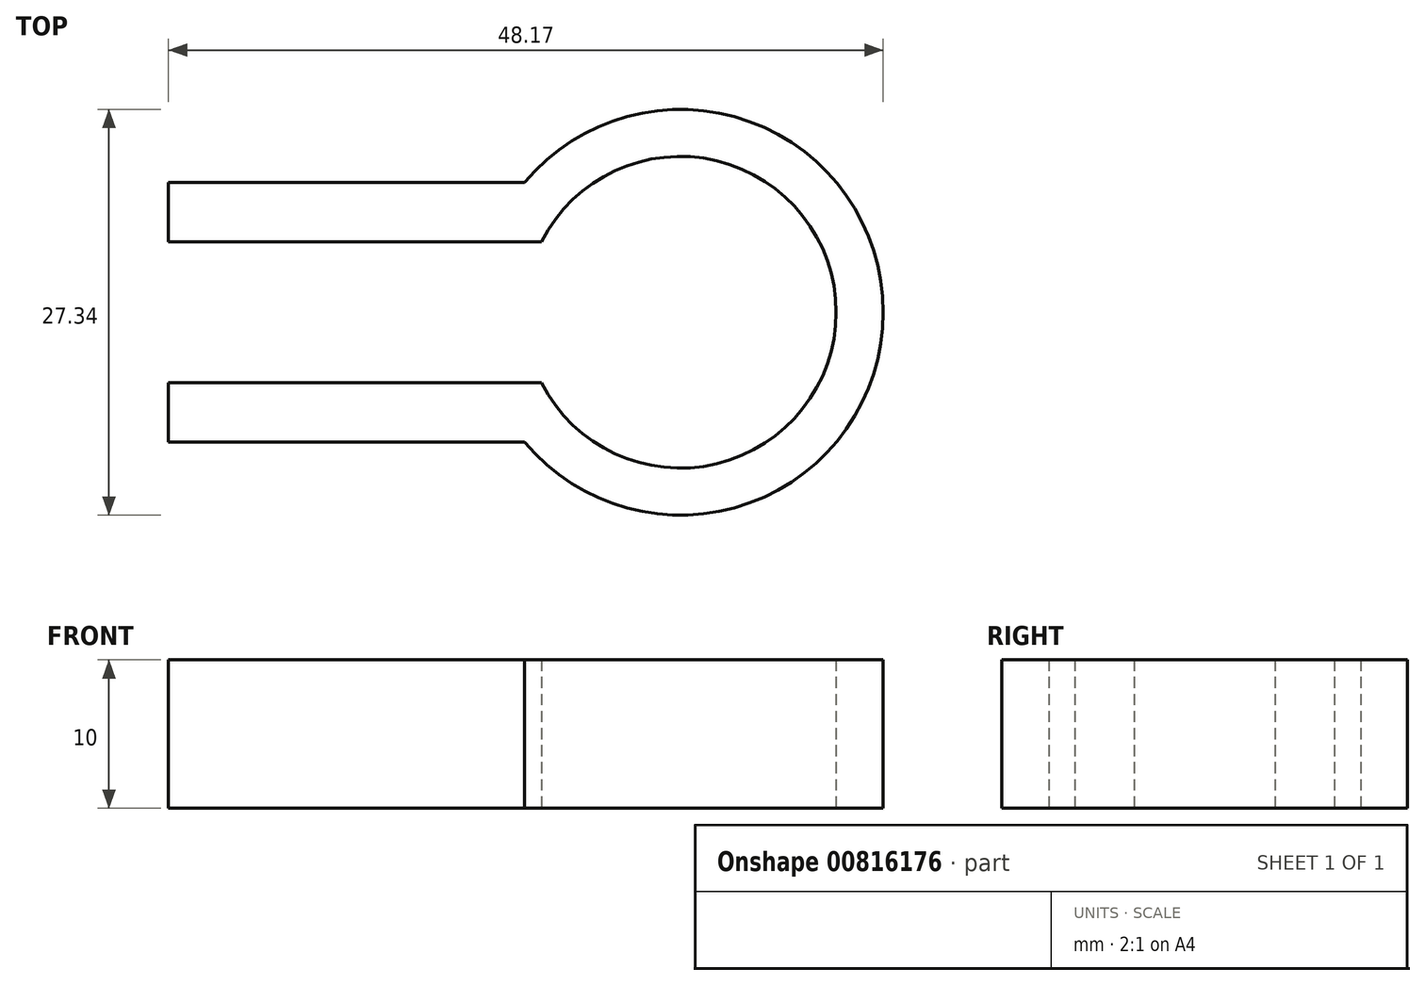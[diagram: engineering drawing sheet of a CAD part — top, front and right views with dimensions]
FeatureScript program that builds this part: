
annotation { "Feature Type Name" : "Feature", "Feature Type Description" : "" }
export const myFeature = defineFeature(function(context is Context, id is Id, definition is map)
    precondition{}
    {
        {
            var Q0;
            Q0=qCreatedBy(makeId("Top.planeOp"),FACE);
            var sketch = newSketch(context, id + "F0", { "sketchPlane" : qUnion([Q0])});
            skLineSegment(sketch, "E0.bottom", {"start": v(-24, 9.5) * mm, "end": v(0, 9.5) * mm});
            skLineSegment(sketch, "E0.top", {"start": v(-24, 0) * mm, "end": v(0, 0) * mm});
            skLineSegment(sketch, "E0.left", {"start": v(-24, 9.5) * mm, "end": v(-24, 0) * mm});
            skLineSegment(sketch, "E0.right", {"start": v(0, 9.5) * mm, "end": v(0, 0) * mm});
            skLineSegment(sketch, "E1.top", {"start": v(-24, -4) * mm, "end": v(0, -4) * mm});
            skLineSegment(sketch, "E1.left", {"start": v(-24, 0) * mm, "end": v(-24, -4) * mm});
            skLineSegment(sketch, "E1.right", {"start": v(0, 0) * mm, "end": v(0, -4) * mm});
            skLineSegment(sketch, "E2.top", {"start": v(-24, 13.5) * mm, "end": v(0, 13.5) * mm});
            skLineSegment(sketch, "E2.left", {"start": v(-24, 9.5) * mm, "end": v(-24, 13.5) * mm});
            skLineSegment(sketch, "E2.right", {"start": v(0, 9.5) * mm, "end": v(0, 13.5) * mm});
            skCircle(sketch, "E3", {"center": v(10.5, 4.75) * mm, "radius": 10.5 * mm});
            skLineSegment(sketch, "E4.bottom", {"start": v(-24, 9.5) * mm, "end": v(-16, 9.5) * mm});
            skLineSegment(sketch, "E4.top", {"start": v(-24, 6.5) * mm, "end": v(-16, 6.5) * mm});
            skLineSegment(sketch, "E4.left", {"start": v(-24, 9.5) * mm, "end": v(-24, 6.5) * mm});
            skLineSegment(sketch, "E4.right", {"start": v(-16, 9.5) * mm, "end": v(-16, 6.5) * mm});
            skCircle(sketch, "E5", {"center": v(10.5, 4.75) * mm, "radius": 13.67 * mm});
            skLineSegment(sketch, "E6", {"start": v(0, 0) * mm, "end": v(1.14, 0) * mm});
            skLineSegment(sketch, "E7", {"start": v(0, 9.5) * mm, "end": v(1.14, 9.5) * mm});
            skLineSegment(sketch, "E8", {"start": v(10.5, 4.75) * mm, "end": v(0, 9.5) * mm});
            skLineSegment(sketch, "E9", {"start": v(0, 0) * mm, "end": v(10.5, 4.75) * mm});
            skSolve(sketch);
        }
        {
            var Q0;
            {var subQ4=sQuery(id+"F0.wireOp",EDGE,"E1.top");Q0=makeQuery(id+"F0.imprint","IMPRINT",FACE,{"disambiguationData":[TD([[makeQuery(id+"F0.imprint","IMPRINT",EDGE,{"derivedFrom":subQ4}),1.0]])]});}
            var Q1;
            {var subQ1=sQuery(id+"F0.wireOp",EDGE,"E2.top");Q1=makeQuery(id+"F0.imprint","IMPRINT",FACE,{"disambiguationData":[TD([[makeQuery(id+"F0.imprint","IMPRINT",EDGE,{"derivedFrom":subQ1}),-1.0]])]});}
            var Q2;
            Q2=makeQuery(id+"F0.imprint","IMPRINT",FACE,{"disambiguationData":[TD([[makeQuery(id+"F0.imprint","IMPRINT",EDGE,{"derivedFrom":sQuery(id+"F0.wireOp",EDGE,"E4.bottom")}),-1.0]])]});
            var Q3;
            {var subQ0=sQuery(id+"F0.wireOp",EDGE,"E2.right");Q3=makeQuery(id+"F0.imprint","IMPRINT",FACE,{"disambiguationData":[TD([[makeQuery(id+"F0.imprint","IMPRINT",EDGE,{"derivedFrom":subQ0}),1.0]])]});}
            var Q4;
            {var subQ1=sQuery(id+"F0.wireOp",EDGE,"E1.right");Q4=makeQuery(id+"F0.imprint","IMPRINT",FACE,{"disambiguationData":[TD([[makeQuery(id+"F0.imprint","IMPRINT",EDGE,{"derivedFrom":subQ1}),1.0]])]});}
            var Q5;
            {var subQ0=sQuery(id+"F0.wireOp",EDGE,"E1.right");Q5=makeQuery(id+"F0.imprint","IMPRINT",FACE,{"disambiguationData":[TD([[makeQuery(id+"F0.imprint","IMPRINT",EDGE,{"derivedFrom":subQ0}),-1.0]])]});}
            extrude(context, id + "F1", {"entities" : qUnion([Q0, Q1, Q2, Q3, Q4, Q5]), "depth" : 10 * mm, "offsetDistance" : 25 * mm});
        }
    });
